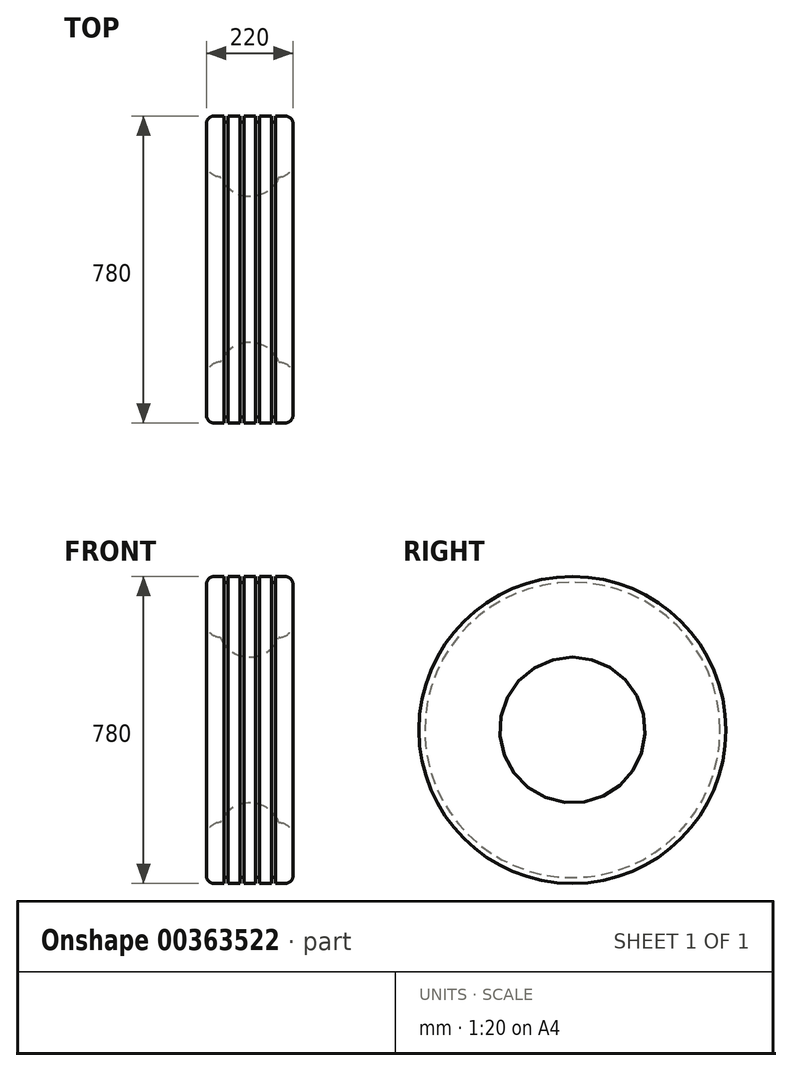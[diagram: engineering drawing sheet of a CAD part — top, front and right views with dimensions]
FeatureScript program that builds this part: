
annotation { "Feature Type Name" : "Feature", "Feature Type Description" : "" }
export const myFeature = defineFeature(function(context is Context, id is Id, definition is map)
    precondition{}
    {
        {
            var Q0;
            Q0=qCreatedBy(makeId("Front.planeOp"),FACE);
            var sketch = newSketch(context, id + "F0", { "sketchPlane" : qUnion([Q0])});
            skLineSegment(sketch, "E0", {"start": v(0, 408.83) * mm, "end": v(0, -399.07) * mm, "construction": true});
            skLineSegment(sketch, "E1", {"start": v(-358.93, 0) * mm, "end": v(425.04, 0) * mm, "construction": true});
            skLineSegment(sketch, "E2", {"start": v(25, 375) * mm, "end": v(25, 390) * mm});
            skLineSegment(sketch, "E3", {"start": v(25, 390) * mm, "end": v(55, 390) * mm});
            skLineSegment(sketch, "E4", {"start": v(55, 390) * mm, "end": v(55, 375) * mm});
            skLineSegment(sketch, "E5", {"start": v(55, 375) * mm, "end": v(65, 375) * mm});
            skLineSegment(sketch, "E6", {"start": v(65, 375) * mm, "end": v(65, 390) * mm});
            skLineSegment(sketch, "E7", {"start": v(65, 390) * mm, "end": v(90, 390) * mm});
            skArc(sketch, "E8", {"start": v(90, 390) * mm, "mid": v(104.14, 384.14) * mm, "end": v(110, 370) * mm});
            skLineSegment(sketch, "E9", {"start": v(110, 370) * mm, "end": v(110, 270.84) * mm});
            skArc(sketch, "E10", {"start": v(0, 185) * mm, "mid": v(44.18, 198.3) * mm, "end": v(73.67, 233.8) * mm});
            skArc(sketch, "E11", {"start": v(75.44, 235.02) * mm, "mid": v(99.95, 245.95) * mm, "end": v(110, 270.84) * mm});
            skLineSegment(sketch, "E12", {"start": v(25, 375) * mm, "end": v(15, 375) * mm});
            skLineSegment(sketch, "E13", {"start": v(15, 375) * mm, "end": v(15, 390) * mm});
            skLineSegment(sketch, "E14", {"start": v(15, 390) * mm, "end": v(0, 390) * mm});
            skPoint(sketch, "E15.visualSharp", {"position": v(74.16, 235) * mm});
            skArc(sketch, "E15.filletArc", {"start": v(75.44, 235.02) * mm, "mid": v(74.37, 234.67) * mm, "end": v(73.67, 233.8) * mm});
            skLineSegment(sketch, "E16", {"start": v(0, 185) * mm, "end": v(0, 390) * mm});
            skSolve(sketch);
        }
        {
            var Q0;
            Q0=makeQuery(id+"F0.imprint","IMPRINT",FACE,{"disambiguationData":[TD([[makeQuery(id+"F0.imprint","IMPRINT",EDGE,{"derivedFrom":sQuery(id+"F0.wireOp",EDGE,"E2")}),-1.0]])]});
            var Q1;
            Q1=sQuery(id+"F0.wireOp",EDGE,"E1");
            revolve(context, id + "F1", {"entities" : qUnion([Q0]), "axis" : qUnion([Q1]), "revolveType" : RevolveType.FULL});
        }
        {
            var Q0;
            Q0=makeQuery(id+"F1.opRevolve","SWEPT_BODY",BODY,{"disambiguationData":[OSD([sQuery(id+"F0.wireOp",EDGE,"E2"),sQuery(id+"F0.wireOp",EDGE,"E3"),sQuery(id+"F0.wireOp",EDGE,"E4"),sQuery(id+"F0.wireOp",EDGE,"E5"),sQuery(id+"F0.wireOp",EDGE,"E6"),sQuery(id+"F0.wireOp",EDGE,"E7"),sQuery(id+"F0.wireOp",EDGE,"E8"),sQuery(id+"F0.wireOp",EDGE,"E9"),sQuery(id+"F0.wireOp",EDGE,"E10"),sQuery(id+"F0.wireOp",EDGE,"E11"),sQuery(id+"F0.wireOp",EDGE,"E12"),sQuery(id+"F0.wireOp",EDGE,"E13"),sQuery(id+"F0.wireOp",EDGE,"E14"),sQuery(id+"F0.wireOp",EDGE,"E15.filletArc"),sQuery(id+"F0.wireOp",EDGE,"E16")])]});
            var Q1;
            Q1=makeQuery(id+"F1.opRevolve","SWEPT_FACE",FACE,{"disambiguationData":[OSD([sQuery(id+"F0.wireOp",EDGE,"E16")])]});
            mirror(context, id + "F2", {"operationType" : NewBodyOperationType.ADD, "entities" : qUnion([Q0]), "mirrorPlane" : qUnion([Q1])});
        }
    });
